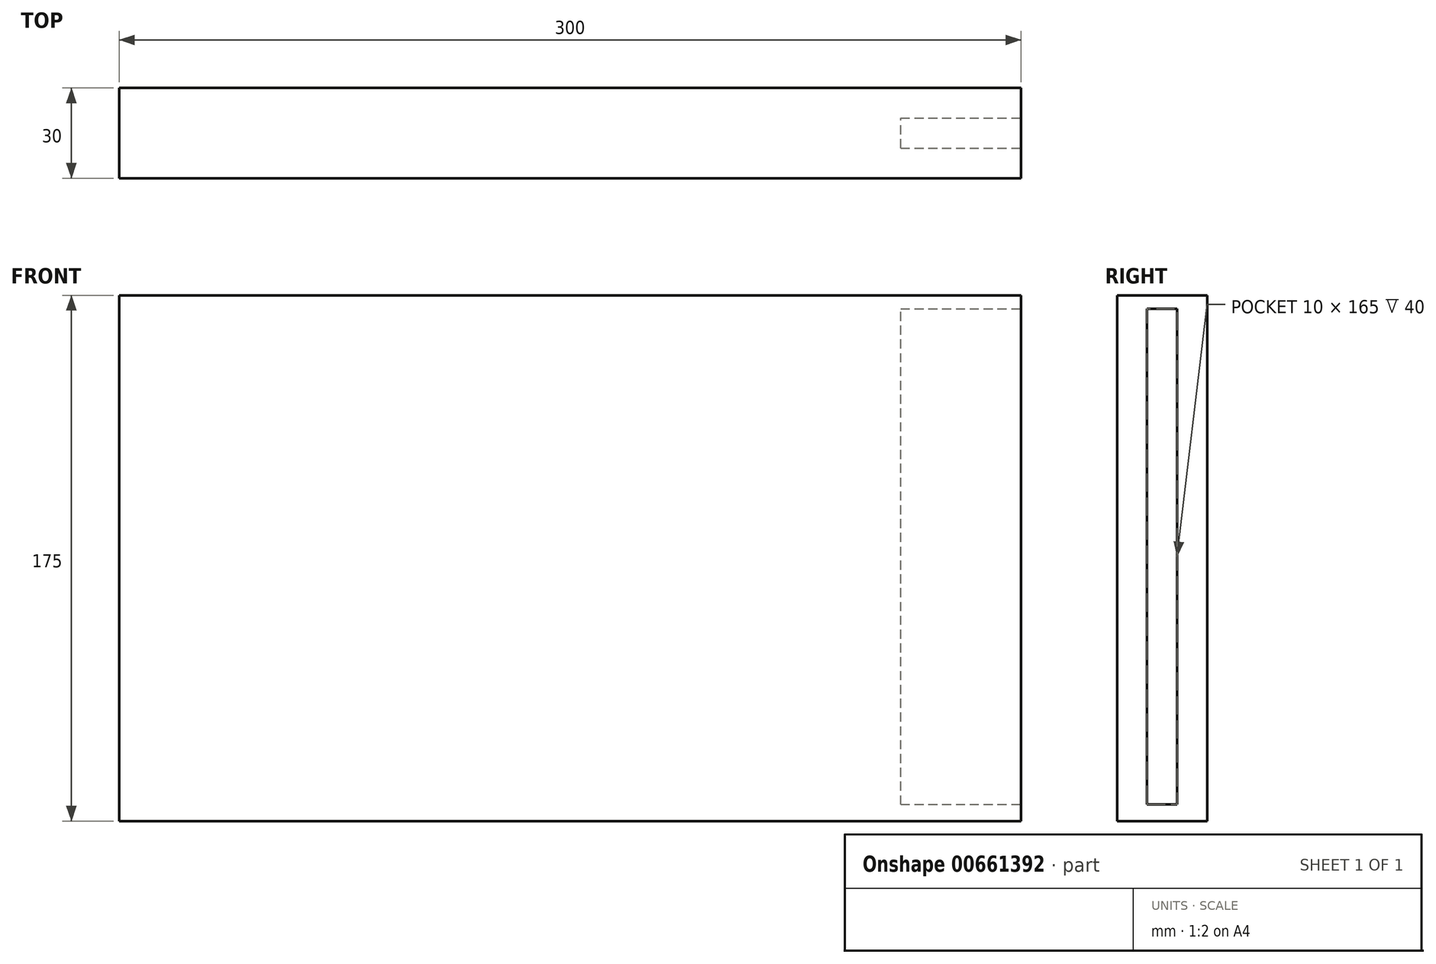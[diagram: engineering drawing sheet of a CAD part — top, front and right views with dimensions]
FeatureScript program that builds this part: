
annotation { "Feature Type Name" : "Feature", "Feature Type Description" : "" }
export const myFeature = defineFeature(function(context is Context, id is Id, definition is map)
    precondition{}
    {
        {
            var Q0;
            Q0=qCreatedBy(makeId("Front.planeOp"),FACE);
            var sketch = newSketch(context, id + "F0", { "sketchPlane" : qUnion([Q0])});
            skLineSegment(sketch, "E0.bottom", {"start": v(150, -87.5) * mm, "end": v(-150, -87.5) * mm});
            skLineSegment(sketch, "E0.top", {"start": v(150, 87.5) * mm, "end": v(-150, 87.5) * mm});
            skLineSegment(sketch, "E0.left", {"start": v(150, -87.5) * mm, "end": v(150, 87.5) * mm});
            skLineSegment(sketch, "E0.right", {"start": v(-150, -87.5) * mm, "end": v(-150, 87.5) * mm});
            skPoint(sketch, "E0.middle", {"position": v(0, 0) * mm});
            skSolve(sketch);
        }
        {
            var Q0;
            Q0=makeQuery(id+"F0.imprint","IMPRINT",FACE,{"disambiguationData":[TD([[makeQuery(id+"F0.imprint","IMPRINT",EDGE,{"derivedFrom":sQuery(id+"F0.wireOp",EDGE,"E0.bottom")}),-1.0]])]});
            extrude(context, id + "F1", {"entities" : qUnion([Q0]), "depth" : 30 * mm, "offsetDistance" : 25 * mm});
        }
        {
            var Q0;
            Q0=makeQuery(id+"F1.opExtrude","SWEPT_FACE",FACE,{"disambiguationData":[OSD([sQuery(id+"F0.wireOp",EDGE,"E0.left")])]});
            var sketch = newSketch(context, id + "F2", { "sketchPlane" : qUnion([Q0])});
            skLineSegment(sketch, "E1.bottom", {"start": v(-20, -82) * mm, "end": v(-10, -82) * mm});
            skLineSegment(sketch, "E1.top", {"start": v(-20, 83) * mm, "end": v(-10, 83) * mm});
            skLineSegment(sketch, "E1.left", {"start": v(-20, -82) * mm, "end": v(-20, 83) * mm});
            skLineSegment(sketch, "E1.right", {"start": v(-10, -82) * mm, "end": v(-10, 83) * mm});
            skLineSegment(sketch, "E2", {"start": v(-30, -82) * mm, "end": v(-20, -82) * mm});
            skLineSegment(sketch, "E3", {"start": v(-30, -87.5) * mm, "end": v(-30, -82) * mm});
            skLineSegment(sketch, "E4", {"start": v(-20, 83) * mm, "end": v(-30, 83) * mm});
            skLineSegment(sketch, "E5", {"start": v(-30, 83) * mm, "end": v(-20, 83) * mm});
            skLineSegment(sketch, "E6", {"start": v(-30, 83) * mm, "end": v(-30, 87.5) * mm});
            skLineSegment(sketch, "E7", {"start": v(-10, 83) * mm, "end": v(0, 83) * mm});
            skSolve(sketch);
        }
        {
            var Q0;
            Q0=makeQuery(id+"F2.imprint","IMPRINT",FACE,{"disambiguationData":[TD([[makeQuery(id+"F2.imprint","IMPRINT",EDGE,{"derivedFrom":sQuery(id+"F2.wireOp",EDGE,"E1.bottom")}),1.0]])]});
            extrude(context, id + "F3", {"entities" : qUnion([Q0]), "operationType" : NewBodyOperationType.REMOVE, "oppositeDirection" : true, "depth" : 40 * mm, "offsetDistance" : 25 * mm});
        }
    });
